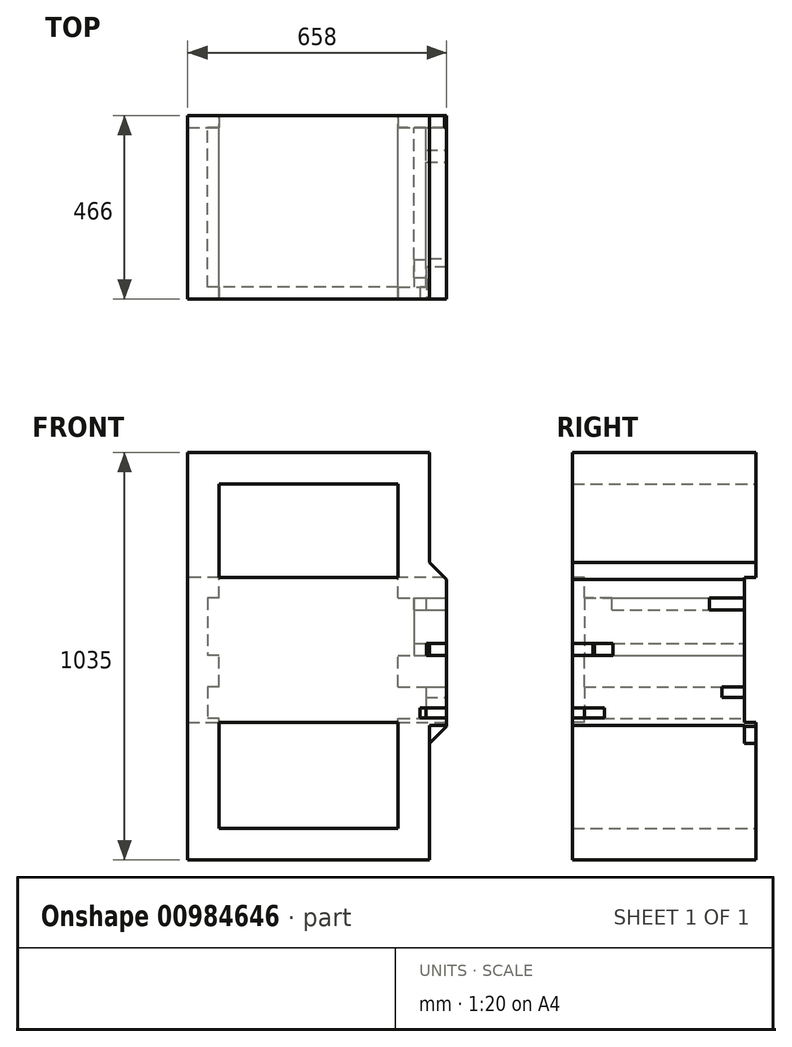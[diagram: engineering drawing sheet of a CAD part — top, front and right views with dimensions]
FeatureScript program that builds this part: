
annotation { "Feature Type Name" : "Feature", "Feature Type Description" : "" }
export const myFeature = defineFeature(function(context is Context, id is Id, definition is map)
    precondition{}
    {
        {
            var Q0;
            Q0=qCreatedBy(makeId("Front.planeOp"),FACE);
            var sketch = newSketch(context, id + "F0", { "sketchPlane" : qUnion([Q0])});
            skLineSegment(sketch, "E0", {"start": v(-307.5, 0) * mm, "end": v(307.5, 0) * mm});
            skLineSegment(sketch, "E1", {"start": v(-307.5, 0) * mm, "end": v(-307.5, 1035) * mm});
            skLineSegment(sketch, "E2", {"start": v(-307.5, 1035) * mm, "end": v(307.5, 1035) * mm});
            skLineSegment(sketch, "E3", {"start": v(307.5, 1035) * mm, "end": v(307.5, 0) * mm});
            skLineSegment(sketch, "E4.bottom", {"start": v(-227.5, 80) * mm, "end": v(227.5, 80) * mm});
            skLineSegment(sketch, "E4.top", {"start": v(-227.5, 955) * mm, "end": v(227.5, 955) * mm});
            skLineSegment(sketch, "E4.left", {"start": v(-227.5, 80) * mm, "end": v(-227.5, 360) * mm});
            skLineSegment(sketch, "E4.right", {"start": v(227.5, 80) * mm, "end": v(227.5, 360) * mm});
            skLineSegment(sketch, "E5.bottom", {"start": v(-227.5, 665) * mm, "end": v(-257.5, 665) * mm});
            skLineSegment(sketch, "E5.top", {"start": v(-227.5, 520) * mm, "end": v(-257.5, 520) * mm});
            skLineSegment(sketch, "E5.right", {"start": v(-257.5, 665) * mm, "end": v(-257.5, 520) * mm});
            skLineSegment(sketch, "E6.bottom", {"start": v(227.5, 665) * mm, "end": v(267.5, 665) * mm});
            skLineSegment(sketch, "E6.top", {"start": v(227.5, 520) * mm, "end": v(267.5, 520) * mm});
            skLineSegment(sketch, "E6.right", {"start": v(267.5, 635) * mm, "end": v(267.5, 550) * mm});
            skLineSegment(sketch, "E7.trimOffspring", {"start": v(227.5, 665) * mm, "end": v(227.5, 955) * mm});
            skLineSegment(sketch, "E8.trimOffspring", {"start": v(-227.5, 665) * mm, "end": v(-227.5, 955) * mm});
            skLineSegment(sketch, "E9.bottom", {"start": v(227.5, 440) * mm, "end": v(297.5, 440) * mm});
            skLineSegment(sketch, "E9.top", {"start": v(227.5, 360) * mm, "end": v(297.5, 360) * mm});
            skLineSegment(sketch, "E9.right", {"start": v(297.5, 440) * mm, "end": v(297.5, 360) * mm});
            skLineSegment(sketch, "E10.bottom", {"start": v(-227.5, 440) * mm, "end": v(-257.5, 440) * mm});
            skLineSegment(sketch, "E10.top", {"start": v(-227.5, 360) * mm, "end": v(-257.5, 360) * mm});
            skLineSegment(sketch, "E10.right", {"start": v(-257.5, 440) * mm, "end": v(-257.5, 360) * mm});
            skLineSegment(sketch, "E11.trimOffspring", {"start": v(227.5, 440) * mm, "end": v(227.5, 520) * mm});
            skLineSegment(sketch, "E12.trimOffspring", {"start": v(-227.5, 440) * mm, "end": v(-227.5, 520) * mm});
            skLineSegment(sketch, "E13.bottom", {"start": v(267.5, 665) * mm, "end": v(297.5, 665) * mm});
            skLineSegment(sketch, "E13.top", {"start": v(267.5, 635) * mm, "end": v(297.5, 635) * mm});
            skLineSegment(sketch, "E13.right", {"start": v(297.5, 665) * mm, "end": v(297.5, 635) * mm});
            skLineSegment(sketch, "E14.bottom", {"start": v(267.5, 550) * mm, "end": v(297.5, 550) * mm});
            skLineSegment(sketch, "E14.top", {"start": v(267.5, 520) * mm, "end": v(297.5, 520) * mm});
            skLineSegment(sketch, "E14.right", {"start": v(297.5, 550) * mm, "end": v(297.5, 520) * mm});
            skLineSegment(sketch, "E15.trimOffspring", {"start": v(267.5, 520) * mm, "end": v(267.5, 520) * mm});
            skSolve(sketch);
        }
        {
            var Q0;
            Q0=makeQuery(id+"F0.imprint","IMPRINT",FACE,{"disambiguationData":[TD([[makeQuery(id+"F0.imprint","IMPRINT",EDGE,{"derivedFrom":sQuery(id+"F0.wireOp",EDGE,"E0")}),1.0]])]});
            extrude(context, id + "F1", {"entities" : qUnion([Q0]), "depth" : 436 * mm, "offsetDistance" : 25 * mm});
        }
        {
            var Q0;
            Q0=makeQuery(id+"F1.opExtrude","SWEPT_FACE",FACE,{"disambiguationData":[OSD([sQuery(id+"F0.wireOp",EDGE,"E3")])]});
            var sketch = newSketch(context, id + "F2", { "sketchPlane" : qUnion([Q0])});
            skLineSegment(sketch, "E16.bottom", {"start": v(-383.78, 550) * mm, "end": v(0, 550) * mm});
            skLineSegment(sketch, "E16.top", {"start": v(-383.78, 520) * mm, "end": v(0, 520) * mm});
            skLineSegment(sketch, "E16.left", {"start": v(-383.78, 550) * mm, "end": v(-383.78, 520) * mm});
            skLineSegment(sketch, "E16.right", {"start": v(0, 550) * mm, "end": v(0, 520) * mm});
            skLineSegment(sketch, "E17.bottom", {"start": v(0, 665) * mm, "end": v(-88.2, 665) * mm});
            skLineSegment(sketch, "E17.top", {"start": v(0, 635) * mm, "end": v(-88.2, 635) * mm});
            skLineSegment(sketch, "E17.left", {"start": v(0, 665) * mm, "end": v(0, 635) * mm});
            skLineSegment(sketch, "E17.right", {"start": v(-88.2, 665) * mm, "end": v(-88.2, 635) * mm});
            skLineSegment(sketch, "E18.0", {"start": v(-436, 550) * mm, "end": v(0, 550) * mm});
            skLineSegment(sketch, "E19.0", {"start": v(-436, 520) * mm, "end": v(0, 520) * mm});
            skLineSegment(sketch, "E20.0", {"start": v(-436, 635) * mm, "end": v(0, 635) * mm});
            skLineSegment(sketch, "E21.0", {"start": v(-436, 665) * mm, "end": v(0, 665) * mm});
            skSolve(sketch);
        }
        {
            var Q0;
            Q0 = qSketchRegion(id + "F2", true);
            extrude(context, id + "F3", {"entities" : qUnion([Q0]), "operationType" : NewBodyOperationType.REMOVE, "endBound" : BoundingType.UP_TO_NEXT, "oppositeDirection" : true, "depth" : 25 * mm, "offsetDistance" : 25 * mm});
        }
        {
            var Q0;
            Q0=makeQuery(id+"F1.opExtrude","SWEPT_FACE",FACE,{"disambiguationData":[OSD([sQuery(id+"F0.wireOp",EDGE,"E3")])]});
            var sketch = newSketch(context, id + "F4", { "sketchPlane" : qUnion([Q0])});
            skLineSegment(sketch, "E22.bottom", {"start": v(-436, 710.09) * mm, "end": v(0, 710.09) * mm});
            skLineSegment(sketch, "E22.top", {"start": v(-436, 341.43) * mm, "end": v(0, 341.43) * mm});
            skLineSegment(sketch, "E22.left", {"start": v(-436, 710.09) * mm, "end": v(-436, 341.43) * mm});
            skLineSegment(sketch, "E22.right", {"start": v(0, 710.09) * mm, "end": v(0, 341.43) * mm});
            skSolve(sketch);
        }
        {
            var Q0;
            Q0 = qSketchRegion(id + "F4", true);
            extrude(context, id + "F5", {"entities" : qUnion([Q0]), "operationType" : NewBodyOperationType.ADD, "depth" : 43 * mm, "offsetDistance" : 25 * mm});
        }
        {
            var Q0;
            Q0=makeQuery(id+"F5.opExtrude","CAP_EDGE",EDGE,{"disambiguationData":[OSD([sQuery(id+"F4.wireOp",EDGE,"E22.bottom")])],"isStart":true});
            var Q1;
            Q1=makeQuery(id+"F5.opExtrude","CAP_EDGE",EDGE,{"disambiguationData":[OSD([sQuery(id+"F4.wireOp",EDGE,"E22.top")])],"isStart":true});
            chamfer(context, id + "F6", {"entities" : qUnion([Q0, Q1]), "width" : 45 * mm, "tangentPropagation" : true});
        }
        {
            var Q0;
            Q0=makeQuery(id+"F5.opExtrude","CAP_FACE",FACE,{"disambiguationData":[OSD([sQuery(id+"F4.wireOp",EDGE,"E22.bottom"),sQuery(id+"F4.wireOp",EDGE,"E22.top"),sQuery(id+"F4.wireOp",EDGE,"E22.left"),sQuery(id+"F4.wireOp",EDGE,"E22.right")])],"isStart":false});
            var sketch = newSketch(context, id + "F7", { "sketchPlane" : qUnion([Q0])});
            skLineSegment(sketch, "E23.0", {"start": v(-436, 550) * mm, "end": v(0, 550) * mm, "construction": true});
            skLineSegment(sketch, "E24.0", {"start": v(-436, 520) * mm, "end": v(0, 520) * mm, "construction": true});
            skLineSegment(sketch, "E25", {"start": v(-333.35, 550) * mm, "end": v(-436, 550) * mm});
            skLineSegment(sketch, "E26", {"start": v(-333.35, 520) * mm, "end": v(-436, 520) * mm});
            skLineSegment(sketch, "E27", {"start": v(-436, 520) * mm, "end": v(-436, 550) * mm});
            skLineSegment(sketch, "E28", {"start": v(-333.35, 520) * mm, "end": v(-333.35, 550) * mm});
            skLineSegment(sketch, "E29.0", {"start": v(-88.2, 665) * mm, "end": v(0, 665) * mm, "construction": true});
            skLineSegment(sketch, "E30.0", {"start": v(-88.2, 635) * mm, "end": v(0, 635) * mm, "construction": true});
            skLineSegment(sketch, "E31.0", {"start": v(-88.2, 665) * mm, "end": v(-88.2, 635) * mm, "construction": true});
            skLineSegment(sketch, "E32", {"start": v(-88.2, 665) * mm, "end": v(0, 665) * mm});
            skLineSegment(sketch, "E33", {"start": v(0, 665) * mm, "end": v(0, 635) * mm});
            skLineSegment(sketch, "E34", {"start": v(0, 635) * mm, "end": v(-88.2, 635) * mm});
            skLineSegment(sketch, "E35", {"start": v(-88.2, 635) * mm, "end": v(-88.2, 665) * mm});
            skLineSegment(sketch, "E36", {"start": v(0, 635) * mm, "end": v(0, 665) * mm});
            skSolve(sketch);
        }
        {
            var Q0;
            Q0=makeQuery(id+"F7.imprint","IMPRINT",FACE,{"disambiguationData":[TD([[makeQuery(id+"F7.imprint","IMPRINT",EDGE,{"derivedFrom":sQuery(id+"F7.wireOp",EDGE,"E25")}),1.0]])]});
            var Q1;
            {var subQ5=sQuery(id+"F7.wireOp",EDGE,"E34");Q1=makeQuery(id+"F7.imprint","IMPRINT",FACE,{"disambiguationData":[TD([[makeQuery(id+"F7.imprint","IMPRINT",EDGE,{"derivedFrom":subQ5}),-1.0]])]});}
            var Q2;
            {var subQ0=sQuery(id+"F7.wireOp",EDGE,"E36");var subQ1=sQuery(id+"F7.wireOp",EDGE,"E32");var subQ2=makeQuery(id+"F7.imprint","INTERSECT",VERTEX,{"derivedFrom":[subQ1,subQ0]});Q2=makeQuery(id+"F7.imprint","IMPRINT",FACE,{"disambiguationData":[TD([[makeQuery(id+"F7.imprint","IMPRINT",EDGE,{"disambiguationData":[TD([[subQ2,1.0]])],"derivedFrom":subQ1}),-1.0]])]});}
            extrude(context, id + "F8", {"entities" : qUnion([Q0, Q1, Q2]), "operationType" : NewBodyOperationType.REMOVE, "oppositeDirection" : true, "depth" : 51 * mm, "offsetDistance" : 25 * mm});
        }
        {
            var Q0;
            Q0=makeQuery(id+"F5.boolean.opBoolean","MERGE",FACE,{"derivedFrom":[makeQuery(id+"F1.opExtrude","CAP_FACE",FACE,{"disambiguationData":[OSD([sQuery(id+"F0.wireOp",EDGE,"E0"),sQuery(id+"F0.wireOp",EDGE,"E1"),sQuery(id+"F0.wireOp",EDGE,"E2"),sQuery(id+"F0.wireOp",EDGE,"E3"),sQuery(id+"F0.wireOp",EDGE,"E4.bottom"),sQuery(id+"F0.wireOp",EDGE,"E4.top"),sQuery(id+"F0.wireOp",EDGE,"E4.left"),sQuery(id+"F0.wireOp",EDGE,"E4.right"),sQuery(id+"F0.wireOp",EDGE,"E5.bottom"),sQuery(id+"F0.wireOp",EDGE,"E5.top"),sQuery(id+"F0.wireOp",EDGE,"E5.right"),sQuery(id+"F0.wireOp",EDGE,"E6.bottom"),sQuery(id+"F0.wireOp",EDGE,"E6.top"),sQuery(id+"F0.wireOp",EDGE,"E6.right"),sQuery(id+"F0.wireOp",EDGE,"E7.trimOffspring"),sQuery(id+"F0.wireOp",EDGE,"E8.trimOffspring"),sQuery(id+"F0.wireOp",EDGE,"E9.bottom"),sQuery(id+"F0.wireOp",EDGE,"E9.top"),sQuery(id+"F0.wireOp",EDGE,"E9.right"),sQuery(id+"F0.wireOp",EDGE,"E10.bottom"),sQuery(id+"F0.wireOp",EDGE,"E10.top"),sQuery(id+"F0.wireOp",EDGE,"E10.right"),sQuery(id+"F0.wireOp",EDGE,"E11.trimOffspring"),sQuery(id+"F0.wireOp",EDGE,"E12.trimOffspring"),sQuery(id+"F0.wireOp",EDGE,"E13.bottom"),sQuery(id+"F0.wireOp",EDGE,"E13.top"),sQuery(id+"F0.wireOp",EDGE,"E13.right"),sQuery(id+"F0.wireOp",EDGE,"E14.bottom"),sQuery(id+"F0.wireOp",EDGE,"E14.top"),sQuery(id+"F0.wireOp",EDGE,"E14.right")])],"isStart":false}),makeQuery(id+"F5.opExtrude","SWEPT_FACE",FACE,{"disambiguationData":[OSD([sQuery(id+"F4.wireOp",EDGE,"E22.left")])]})]});
            var sketch = newSketch(context, id + "F9", { "sketchPlane" : qUnion([Q0])});
            skLineSegment(sketch, "E37.bottom", {"start": v(297.5, 550) * mm, "end": v(267.5, 550) * mm});
            skLineSegment(sketch, "E37.top", {"start": v(297.5, 520) * mm, "end": v(267.5, 520) * mm});
            skLineSegment(sketch, "E37.left", {"start": v(297.5, 550) * mm, "end": v(297.5, 520) * mm});
            skLineSegment(sketch, "E37.right", {"start": v(267.5, 550) * mm, "end": v(267.5, 520) * mm});
            skSolve(sketch);
        }
        {
            var Q0;
            Q0 = qSketchRegion(id + "F9", true);
            extrude(context, id + "F10", {"entities" : qUnion([Q0]), "operationType" : NewBodyOperationType.ADD, "oppositeDirection" : true, "depth" : 55 * mm, "offsetDistance" : 25 * mm});
        }
        {
            var Q0;
            Q0=makeQuery(id+"F10.boolean.opBoolean","MERGE",FACE,{"derivedFrom":[makeQuery(id+"F5.boolean.opBoolean","MERGE",FACE,{"derivedFrom":[makeQuery(id+"F1.opExtrude","CAP_FACE",FACE,{"disambiguationData":[OSD([sQuery(id+"F0.wireOp",EDGE,"E0"),sQuery(id+"F0.wireOp",EDGE,"E1"),sQuery(id+"F0.wireOp",EDGE,"E2"),sQuery(id+"F0.wireOp",EDGE,"E3"),sQuery(id+"F0.wireOp",EDGE,"E4.bottom"),sQuery(id+"F0.wireOp",EDGE,"E4.top"),sQuery(id+"F0.wireOp",EDGE,"E4.left"),sQuery(id+"F0.wireOp",EDGE,"E4.right"),sQuery(id+"F0.wireOp",EDGE,"E5.bottom"),sQuery(id+"F0.wireOp",EDGE,"E5.top"),sQuery(id+"F0.wireOp",EDGE,"E5.right"),sQuery(id+"F0.wireOp",EDGE,"E6.bottom"),sQuery(id+"F0.wireOp",EDGE,"E6.top"),sQuery(id+"F0.wireOp",EDGE,"E6.right"),sQuery(id+"F0.wireOp",EDGE,"E7.trimOffspring"),sQuery(id+"F0.wireOp",EDGE,"E8.trimOffspring"),sQuery(id+"F0.wireOp",EDGE,"E9.bottom"),sQuery(id+"F0.wireOp",EDGE,"E9.top"),sQuery(id+"F0.wireOp",EDGE,"E9.right"),sQuery(id+"F0.wireOp",EDGE,"E10.bottom"),sQuery(id+"F0.wireOp",EDGE,"E10.top"),sQuery(id+"F0.wireOp",EDGE,"E10.right"),sQuery(id+"F0.wireOp",EDGE,"E11.trimOffspring"),sQuery(id+"F0.wireOp",EDGE,"E12.trimOffspring"),sQuery(id+"F0.wireOp",EDGE,"E13.bottom"),sQuery(id+"F0.wireOp",EDGE,"E13.top"),sQuery(id+"F0.wireOp",EDGE,"E13.right"),sQuery(id+"F0.wireOp",EDGE,"E14.bottom"),sQuery(id+"F0.wireOp",EDGE,"E14.top"),sQuery(id+"F0.wireOp",EDGE,"E14.right")])],"isStart":false}),makeQuery(id+"F5.opExtrude","SWEPT_FACE",FACE,{"disambiguationData":[OSD([sQuery(id+"F4.wireOp",EDGE,"E22.left")])]})]}),makeQuery(id+"F10.opExtrude","CAP_FACE",FACE,{"disambiguationData":[OSD([sQuery(id+"F9.wireOp",EDGE,"E37.bottom"),sQuery(id+"F9.wireOp",EDGE,"E37.top"),sQuery(id+"F9.wireOp",EDGE,"E37.left"),sQuery(id+"F9.wireOp",EDGE,"E37.right")])],"isStart":true})]});
            var sketch = newSketch(context, id + "F11", { "sketchPlane" : qUnion([Q0])});
            skLineSegment(sketch, "E38.0", {"start": v(267.5, 635) * mm, "end": v(297.5, 635) * mm});
            skLineSegment(sketch, "E39.0", {"start": v(297.5, 665) * mm, "end": v(297.5, 635) * mm});
            skLineSegment(sketch, "E40", {"start": v(267.5, 635) * mm, "end": v(267.5, 665) * mm});
            skLineSegment(sketch, "E41", {"start": v(267.5, 665) * mm, "end": v(297.5, 665) * mm});
            skSolve(sketch);
        }
        {
            var Q0;
            Q0=makeQuery(id+"F11.imprint","IMPRINT",FACE,{"disambiguationData":[TD([[makeQuery(id+"F11.imprint","IMPRINT",EDGE,{"derivedFrom":sQuery(id+"F11.wireOp",EDGE,"E38.0")}),1.0]])]});
            extrude(context, id + "F12", {"entities" : qUnion([Q0]), "operationType" : NewBodyOperationType.ADD, "oppositeDirection" : true, "depth" : 100 * mm, "offsetDistance" : 25 * mm});
        }
        {
            var Q0;
            Q0=makeQuery(id+"F12.boolean.opBoolean","MERGE",FACE,{"derivedFrom":[makeQuery(id+"F10.boolean.opBoolean","MERGE",FACE,{"derivedFrom":[makeQuery(id+"F5.boolean.opBoolean","MERGE",FACE,{"derivedFrom":[makeQuery(id+"F1.opExtrude","CAP_FACE",FACE,{"disambiguationData":[OSD([sQuery(id+"F0.wireOp",EDGE,"E0"),sQuery(id+"F0.wireOp",EDGE,"E1"),sQuery(id+"F0.wireOp",EDGE,"E2"),sQuery(id+"F0.wireOp",EDGE,"E3"),sQuery(id+"F0.wireOp",EDGE,"E4.bottom"),sQuery(id+"F0.wireOp",EDGE,"E4.top"),sQuery(id+"F0.wireOp",EDGE,"E4.left"),sQuery(id+"F0.wireOp",EDGE,"E4.right"),sQuery(id+"F0.wireOp",EDGE,"E5.bottom"),sQuery(id+"F0.wireOp",EDGE,"E5.top"),sQuery(id+"F0.wireOp",EDGE,"E5.right"),sQuery(id+"F0.wireOp",EDGE,"E6.bottom"),sQuery(id+"F0.wireOp",EDGE,"E6.top"),sQuery(id+"F0.wireOp",EDGE,"E6.right"),sQuery(id+"F0.wireOp",EDGE,"E7.trimOffspring"),sQuery(id+"F0.wireOp",EDGE,"E8.trimOffspring"),sQuery(id+"F0.wireOp",EDGE,"E9.bottom"),sQuery(id+"F0.wireOp",EDGE,"E9.top"),sQuery(id+"F0.wireOp",EDGE,"E9.right"),sQuery(id+"F0.wireOp",EDGE,"E10.bottom"),sQuery(id+"F0.wireOp",EDGE,"E10.top"),sQuery(id+"F0.wireOp",EDGE,"E10.right"),sQuery(id+"F0.wireOp",EDGE,"E11.trimOffspring"),sQuery(id+"F0.wireOp",EDGE,"E12.trimOffspring"),sQuery(id+"F0.wireOp",EDGE,"E13.bottom"),sQuery(id+"F0.wireOp",EDGE,"E13.top"),sQuery(id+"F0.wireOp",EDGE,"E13.right"),sQuery(id+"F0.wireOp",EDGE,"E14.bottom"),sQuery(id+"F0.wireOp",EDGE,"E14.top"),sQuery(id+"F0.wireOp",EDGE,"E14.right")])],"isStart":false}),makeQuery(id+"F5.opExtrude","SWEPT_FACE",FACE,{"disambiguationData":[OSD([sQuery(id+"F4.wireOp",EDGE,"E22.left")])]})]}),makeQuery(id+"F10.opExtrude","CAP_FACE",FACE,{"disambiguationData":[OSD([sQuery(id+"F9.wireOp",EDGE,"E37.bottom"),sQuery(id+"F9.wireOp",EDGE,"E37.top"),sQuery(id+"F9.wireOp",EDGE,"E37.left"),sQuery(id+"F9.wireOp",EDGE,"E37.right")])],"isStart":true})]}),makeQuery(id+"F12.opExtrude","CAP_FACE",FACE,{"disambiguationData":[OSD([sQuery(id+"F11.wireOp",EDGE,"E38.0"),sQuery(id+"F11.wireOp",EDGE,"E39.0"),sQuery(id+"F11.wireOp",EDGE,"E40"),sQuery(id+"F11.wireOp",EDGE,"E41")])],"isStart":true})]});
            var sketch = newSketch(context, id + "F13", { "sketchPlane" : qUnion([Q0])});
            skLineSegment(sketch, "E42.bottom", {"start": v(297.82, 717.92) * mm, "end": v(-289.37, 717.92) * mm});
            skLineSegment(sketch, "E42.top", {"start": v(297.82, 348.85) * mm, "end": v(-289.37, 348.85) * mm});
            skLineSegment(sketch, "E42.left", {"start": v(297.82, 717.92) * mm, "end": v(297.82, 348.85) * mm});
            skLineSegment(sketch, "E42.right", {"start": v(-289.37, 717.92) * mm, "end": v(-289.37, 348.85) * mm});
            skSolve(sketch);
        }
        {
            var Q0;
            {var subQ2=makeQuery(id+"F1.opExtrude","CAP_EDGE",EDGE,{"disambiguationData":[OSD([sQuery(id+"F0.wireOp",EDGE,"E5.bottom")])],"isStart":false});Q0=makeQuery(id+"F13.imprint","IMPRINT",FACE,{"disambiguationData":[TD([[makeQuery(id+"F13.imprint","IMPRINT",EDGE,{"derivedFrom":subQ2}),1.0]])]});}
            extrude(context, id + "F14", {"entities" : qUnion([Q0]), "operationType" : NewBodyOperationType.ADD, "oppositeDirection" : true, "depth" : 30 * mm, "offsetDistance" : 25 * mm});
        }
        {
            var Q0;
            {var subQ0=sQuery(id+"F0.wireOp",EDGE,"E11.trimOffspring");var subQ1=sQuery(id+"F0.wireOp",EDGE,"E10.top");var subQ2=sQuery(id+"F0.wireOp",EDGE,"E10.bottom");var subQ3=sQuery(id+"F0.wireOp",EDGE,"E9.right");var subQ4=sQuery(id+"F0.wireOp",EDGE,"E9.top");var subQ5=sQuery(id+"F0.wireOp",EDGE,"E9.bottom");var subQ6=sQuery(id+"F0.wireOp",EDGE,"E8.trimOffspring");var subQ7=sQuery(id+"F0.wireOp",EDGE,"E7.trimOffspring");var subQ8=sQuery(id+"F0.wireOp",EDGE,"E14.top");var subQ9=sQuery(id+"F0.wireOp",EDGE,"E6.top");var subQ10=sQuery(id+"F0.wireOp",EDGE,"E13.bottom");var subQ11=sQuery(id+"F0.wireOp",EDGE,"E6.bottom");var subQ12=sQuery(id+"F0.wireOp",EDGE,"E5.right");var subQ13=sQuery(id+"F0.wireOp",EDGE,"E2");var subQ14=sQuery(id+"F0.wireOp",EDGE,"E1");var subQ15=sQuery(id+"F0.wireOp",EDGE,"E3");var subQ17=sQuery(id+"F0.wireOp",EDGE,"E10.right");var subQ18=sQuery(id+"F0.wireOp",EDGE,"E0");var subQ19=sQuery(id+"F0.wireOp",EDGE,"E5.top");var subQ20=sQuery(id+"F0.wireOp",EDGE,"E4.bottom");var subQ21=sQuery(id+"F0.wireOp",EDGE,"E4.top");var subQ22=sQuery(id+"F0.wireOp",EDGE,"E4.left");var subQ23=sQuery(id+"F0.wireOp",EDGE,"E4.right");var subQ24=sQuery(id+"F0.wireOp",EDGE,"E5.bottom");var subQ25=sQuery(id+"F0.wireOp",EDGE,"E12.trimOffspring");var subQ26=sQuery(id+"F0.wireOp",EDGE,"E14.bottom");var subQ27=sQuery(id+"F0.wireOp",EDGE,"E13.top");var subQ28=sQuery(id+"F0.wireOp",EDGE,"E6.right");var subQ29=makeQuery(id+"F1.opExtrude","CAP_FACE",FACE,{"disambiguationData":[OSD([subQ18,subQ14,subQ13,subQ15,subQ20,subQ21,subQ22,subQ23,subQ24,subQ19,subQ12,subQ11,subQ9,subQ28,subQ7,subQ6,subQ5,subQ4,subQ3,subQ2,subQ1,subQ17,subQ0,subQ25,subQ10,subQ27,sQuery(id+"F0.wireOp",EDGE,"E13.right"),subQ26,subQ8,sQuery(id+"F0.wireOp",EDGE,"E14.right")])],"isStart":true});Q0=makeQuery(id+"F5.boolean.opBoolean","MERGE",FACE,{"derivedFrom":[makeQuery(id+"F3.boolean.opBoolean","SPLIT",FACE,{"disambiguationData":[TD([makeQuery(id+"F1.opExtrude","SWEPT_FACE",FACE,{"disambiguationData":[OSD([subQ28])]})])],"derivedFrom":subQ29}),makeQuery(id+"F3.boolean.opBoolean","SPLIT",FACE,{"disambiguationData":[TD([makeQuery(id+"F1.opExtrude","SWEPT_FACE",FACE,{"disambiguationData":[OSD([subQ18])]})])],"derivedFrom":subQ29}),makeQuery(id+"F5.opExtrude","SWEPT_FACE",FACE,{"disambiguationData":[OSD([sQuery(id+"F4.wireOp",EDGE,"E22.right")])]})]});}
            var sketch = newSketch(context, id + "F15", { "sketchPlane" : qUnion([Q0])});
            skLineSegment(sketch, "E43.bottom", {"start": v(-297.5, 440) * mm, "end": v(-350.5, 440) * mm});
            skLineSegment(sketch, "E43.top", {"start": v(-297.5, 412.74) * mm, "end": v(-350.5, 412.74) * mm});
            skLineSegment(sketch, "E43.left", {"start": v(-297.5, 440) * mm, "end": v(-297.5, 412.74) * mm});
            skLineSegment(sketch, "E43.right", {"start": v(-350.5, 440) * mm, "end": v(-350.5, 412.74) * mm});
            skSolve(sketch);
        }
        {
            var Q0;
            Q0=makeQuery(id+"F15.imprint","IMPRINT",FACE,{"disambiguationData":[TD([[makeQuery(id+"F15.imprint","IMPRINT",EDGE,{"derivedFrom":sQuery(id+"F15.wireOp",EDGE,"E43.bottom")}),1.0]])]});
            extrude(context, id + "F16", {"entities" : qUnion([Q0]), "operationType" : NewBodyOperationType.REMOVE, "oppositeDirection" : true, "depth" : 57 * mm, "offsetDistance" : 25 * mm});
        }
        {
            var Q0;
            {var subQ0=sQuery(id+"F11.wireOp",EDGE,"E40");var subQ1=sQuery(id+"F9.wireOp",EDGE,"E37.right");var subQ2=sQuery(id+"F0.wireOp",EDGE,"E14.top");var subQ3=sQuery(id+"F0.wireOp",EDGE,"E13.bottom");var subQ4=sQuery(id+"F0.wireOp",EDGE,"E12.trimOffspring");var subQ5=sQuery(id+"F0.wireOp",EDGE,"E11.trimOffspring");var subQ6=sQuery(id+"F0.wireOp",EDGE,"E10.right");var subQ7=sQuery(id+"F0.wireOp",EDGE,"E10.top");var subQ8=sQuery(id+"F0.wireOp",EDGE,"E10.bottom");var subQ9=sQuery(id+"F0.wireOp",EDGE,"E9.right");var subQ10=sQuery(id+"F0.wireOp",EDGE,"E9.top");var subQ11=sQuery(id+"F0.wireOp",EDGE,"E9.bottom");var subQ12=sQuery(id+"F0.wireOp",EDGE,"E8.trimOffspring");var subQ13=sQuery(id+"F0.wireOp",EDGE,"E7.trimOffspring");var subQ14=sQuery(id+"F0.wireOp",EDGE,"E6.right");var subQ15=sQuery(id+"F0.wireOp",EDGE,"E6.top");var subQ16=sQuery(id+"F0.wireOp",EDGE,"E6.bottom");var subQ17=sQuery(id+"F0.wireOp",EDGE,"E5.right");var subQ18=sQuery(id+"F0.wireOp",EDGE,"E5.top");var subQ19=sQuery(id+"F0.wireOp",EDGE,"E5.bottom");var subQ20=sQuery(id+"F0.wireOp",EDGE,"E4.right");var subQ21=sQuery(id+"F0.wireOp",EDGE,"E4.left");Q0=makeQuery(id+"F14.boolean.opBoolean","MERGE",FACE,{"derivedFrom":[makeQuery(id+"F12.boolean.opBoolean","MERGE",FACE,{"derivedFrom":[makeQuery(id+"F10.boolean.opBoolean","MERGE",FACE,{"derivedFrom":[makeQuery(id+"F5.boolean.opBoolean","MERGE",FACE,{"derivedFrom":[makeQuery(id+"F1.opExtrude","CAP_FACE",FACE,{"disambiguationData":[OSD([sQuery(id+"F0.wireOp",EDGE,"E0"),sQuery(id+"F0.wireOp",EDGE,"E1"),sQuery(id+"F0.wireOp",EDGE,"E2"),sQuery(id+"F0.wireOp",EDGE,"E3"),sQuery(id+"F0.wireOp",EDGE,"E4.bottom"),sQuery(id+"F0.wireOp",EDGE,"E4.top"),subQ21,subQ20,subQ19,subQ18,subQ17,subQ16,subQ15,subQ14,subQ13,subQ12,subQ11,subQ10,subQ9,subQ8,subQ7,subQ6,subQ5,subQ4,subQ3,sQuery(id+"F0.wireOp",EDGE,"E13.top"),sQuery(id+"F0.wireOp",EDGE,"E13.right"),sQuery(id+"F0.wireOp",EDGE,"E14.bottom"),subQ2,sQuery(id+"F0.wireOp",EDGE,"E14.right")])],"isStart":false}),makeQuery(id+"F5.opExtrude","SWEPT_FACE",FACE,{"disambiguationData":[OSD([sQuery(id+"F4.wireOp",EDGE,"E22.left")])]})]}),makeQuery(id+"F10.opExtrude","CAP_FACE",FACE,{"disambiguationData":[OSD([sQuery(id+"F9.wireOp",EDGE,"E37.bottom"),sQuery(id+"F9.wireOp",EDGE,"E37.top"),sQuery(id+"F9.wireOp",EDGE,"E37.left"),subQ1])],"isStart":true})]}),makeQuery(id+"F12.opExtrude","CAP_FACE",FACE,{"disambiguationData":[OSD([sQuery(id+"F11.wireOp",EDGE,"E38.0"),sQuery(id+"F11.wireOp",EDGE,"E39.0"),subQ0,sQuery(id+"F11.wireOp",EDGE,"E41")])],"isStart":true})]}),makeQuery(id+"F14.opExtrude","CAP_FACE",FACE,{"disambiguationData":[OSD([subQ21,subQ20,subQ19,subQ18,subQ17,subQ16,subQ15,subQ14,subQ13,subQ12,subQ11,subQ10,subQ9,subQ8,subQ7,subQ6,subQ5,subQ4,subQ3,subQ2,subQ1,subQ0,sQuery(id+"F13.wireOp",EDGE,"E42.bottom"),sQuery(id+"F13.wireOp",EDGE,"E42.top")])],"isStart":true})]});}
            var sketch = newSketch(context, id + "F17", { "sketchPlane" : qUnion([Q0])});
            skLineSegment(sketch, "E44.bottom", {"start": v(350.5, 361.17) * mm, "end": v(282.57, 361.17) * mm});
            skLineSegment(sketch, "E44.top", {"start": v(350.5, 386.53) * mm, "end": v(282.57, 386.53) * mm});
            skLineSegment(sketch, "E44.left", {"start": v(350.5, 361.17) * mm, "end": v(350.5, 386.53) * mm});
            skLineSegment(sketch, "E44.right", {"start": v(282.57, 361.17) * mm, "end": v(282.57, 386.53) * mm});
            skSolve(sketch);
        }
        {
            var Q0;
            Q0=makeQuery(id+"F17.imprint","IMPRINT",FACE,{"disambiguationData":[TD([[makeQuery(id+"F17.imprint","IMPRINT",EDGE,{"derivedFrom":sQuery(id+"F17.wireOp",EDGE,"E44.bottom")}),-1.0]])]});
            extrude(context, id + "F18", {"entities" : qUnion([Q0]), "operationType" : NewBodyOperationType.REMOVE, "oppositeDirection" : true, "depth" : 81 * mm, "offsetDistance" : 25 * mm});
        }
        {
            var Q0;
            {var subQ0=sQuery(id+"F0.wireOp",EDGE,"E12.trimOffspring");var subQ2=sQuery(id+"F0.wireOp",EDGE,"E10.top");var subQ4=sQuery(id+"F0.wireOp",EDGE,"E10.bottom");var subQ6=sQuery(id+"F0.wireOp",EDGE,"E9.right");var subQ8=sQuery(id+"F4.wireOp",EDGE,"E22.right");var subQ11=sQuery(id+"F0.wireOp",EDGE,"E9.top");var subQ13=sQuery(id+"F0.wireOp",EDGE,"E8.trimOffspring");var subQ15=sQuery(id+"F0.wireOp",EDGE,"E7.trimOffspring");var subQ17=sQuery(id+"F0.wireOp",EDGE,"E13.bottom");var subQ18=sQuery(id+"F0.wireOp",EDGE,"E6.bottom");var subQ20=sQuery(id+"F0.wireOp",EDGE,"E5.right");var subQ22=sQuery(id+"F0.wireOp",EDGE,"E2");var subQ24=sQuery(id+"F0.wireOp",EDGE,"E1");var subQ26=sQuery(id+"F0.wireOp",EDGE,"E3");var subQ28=sQuery(id+"F0.wireOp",EDGE,"E10.right");var subQ30=sQuery(id+"F0.wireOp",EDGE,"E0");var subQ31=makeQuery(id+"F1.opExtrude","SWEPT_FACE",FACE,{"disambiguationData":[OSD([subQ30])]});var subQ32=sQuery(id+"F0.wireOp",EDGE,"E5.top");var subQ34=sQuery(id+"F0.wireOp",EDGE,"E4.bottom");var subQ36=sQuery(id+"F0.wireOp",EDGE,"E4.top");var subQ38=sQuery(id+"F0.wireOp",EDGE,"E4.left");var subQ40=sQuery(id+"F0.wireOp",EDGE,"E4.right");var subQ42=sQuery(id+"F0.wireOp",EDGE,"E5.bottom");var subQ44=sQuery(id+"F0.wireOp",EDGE,"E11.trimOffspring");var subQ45=sQuery(id+"F0.wireOp",EDGE,"E9.bottom");var subQ46=sQuery(id+"F0.wireOp",EDGE,"E14.top");var subQ47=sQuery(id+"F0.wireOp",EDGE,"E6.top");var subQ48=sQuery(id+"F0.wireOp",EDGE,"E14.bottom");var subQ49=sQuery(id+"F0.wireOp",EDGE,"E13.top");var subQ50=sQuery(id+"F0.wireOp",EDGE,"E6.right");var subQ51=makeQuery(id+"F1.opExtrude","CAP_FACE",FACE,{"disambiguationData":[OSD([subQ30,subQ24,subQ22,subQ26,subQ34,subQ36,subQ38,subQ40,subQ42,subQ32,subQ20,subQ18,subQ47,subQ50,subQ15,subQ13,subQ45,subQ11,subQ6,subQ4,subQ2,subQ28,subQ44,subQ0,subQ17,subQ49,sQuery(id+"F0.wireOp",EDGE,"E13.right"),subQ48,subQ46,sQuery(id+"F0.wireOp",EDGE,"E14.right")])],"isStart":true});Q0=makeQuery(id+"F16.boolean.opBoolean","SPLIT",FACE,{"disambiguationData":[TD([subQ31])],"derivedFrom":makeQuery(id+"F5.boolean.opBoolean","MERGE",FACE,{"derivedFrom":[makeQuery(id+"F3.boolean.opBoolean","SPLIT",FACE,{"disambiguationData":[TD([makeQuery(id+"F1.opExtrude","SWEPT_FACE",FACE,{"disambiguationData":[OSD([subQ50])]})])],"derivedFrom":subQ51}),makeQuery(id+"F3.boolean.opBoolean","SPLIT",FACE,{"disambiguationData":[TD([subQ31])],"derivedFrom":subQ51}),makeQuery(id+"F5.opExtrude","SWEPT_FACE",FACE,{"disambiguationData":[OSD([subQ8])]})]})});}
            var sketch = newSketch(context, id + "F19", { "sketchPlane" : qUnion([Q0])});
            skLineSegment(sketch, "E45.0", {"start": v(-227.5, 348.85) * mm, "end": v(227.5, 348.85) * mm, "construction": true});
            skLineSegment(sketch, "E46.0", {"start": v(-227.5, 717.92) * mm, "end": v(227.5, 717.92) * mm, "construction": true});
            skLineSegment(sketch, "E47", {"start": v(-227.5, 717.92) * mm, "end": v(-227.5, 955) * mm});
            skLineSegment(sketch, "E48", {"start": v(-227.5, 955) * mm, "end": v(227.5, 955) * mm});
            skLineSegment(sketch, "E49", {"start": v(227.5, 955) * mm, "end": v(227.5, 717.92) * mm});
            skLineSegment(sketch, "E50", {"start": v(227.5, 717.92) * mm, "end": v(307.5, 717.92) * mm});
            skLineSegment(sketch, "E51", {"start": v(307.5, 717.92) * mm, "end": v(307.5, 1035) * mm});
            skLineSegment(sketch, "E52", {"start": v(307.5, 1035) * mm, "end": v(-307.5, 1035) * mm});
            skLineSegment(sketch, "E53", {"start": v(-307.5, 1035) * mm, "end": v(-307.5, 755.09) * mm});
            skLineSegment(sketch, "E54", {"start": v(-307.5, 755.09) * mm, "end": v(-350.5, 712.09) * mm});
            skLineSegment(sketch, "E55", {"start": v(-350.5, 717.92) * mm, "end": v(-350.5, 712.09) * mm});
            skLineSegment(sketch, "E56", {"start": v(-350.5, 717.92) * mm, "end": v(-227.5, 717.92) * mm});
            skLineSegment(sketch, "E57", {"start": v(-227.5, 348.85) * mm, "end": v(-359.91, 348.85) * mm});
            skLineSegment(sketch, "E58", {"start": v(-359.91, 348.85) * mm, "end": v(-307.5, 296.43) * mm});
            skLineSegment(sketch, "E59", {"start": v(-307.5, 296.43) * mm, "end": v(-307.5, 0) * mm});
            skLineSegment(sketch, "E60", {"start": v(-307.5, 0) * mm, "end": v(307.5, 0) * mm});
            skLineSegment(sketch, "E61", {"start": v(307.5, 0) * mm, "end": v(307.5, 348.85) * mm});
            skLineSegment(sketch, "E62", {"start": v(307.5, 348.85) * mm, "end": v(227.5, 348.85) * mm});
            skLineSegment(sketch, "E63", {"start": v(227.5, 348.85) * mm, "end": v(227.5, 80) * mm});
            skLineSegment(sketch, "E64", {"start": v(227.5, 80) * mm, "end": v(-227.5, 80) * mm});
            skLineSegment(sketch, "E65", {"start": v(-227.5, 80) * mm, "end": v(-227.5, 348.85) * mm});
            skSolve(sketch);
        }
        {
            var Q0;
            Q0=makeQuery(id+"F19.imprint","IMPRINT",FACE,{"disambiguationData":[TD([[makeQuery(id+"F19.imprint","IMPRINT",EDGE,{"derivedFrom":sQuery(id+"F19.wireOp",EDGE,"E57")}),1.0]])]});
            var Q1;
            Q1=makeQuery(id+"F19.imprint","IMPRINT",FACE,{"disambiguationData":[TD([[makeQuery(id+"F19.imprint","IMPRINT",EDGE,{"derivedFrom":sQuery(id+"F19.wireOp",EDGE,"E47")}),1.0]])]});
            var Q2;
            {var subQ0=sQuery(id+"F19.wireOp",EDGE,"E59");Q2=makeQuery(id+"F19.imprint","IMPRINT",FACE,{"disambiguationData":[TD([[makeQuery(id+"F19.imprint","IMPRINT",EDGE,{"derivedFrom":subQ0}),1.0]])]});}
            extrude(context, id + "F20", {"entities" : qUnion([Q0, Q1, Q2]), "operationType" : NewBodyOperationType.ADD, "depth" : 30 * mm, "offsetDistance" : 25 * mm});
        }
        {
            var Q0;
            Q0=makeQuery(id+"F5.opExtrude","CAP_FACE",FACE,{"disambiguationData":[OSD([sQuery(id+"F4.wireOp",EDGE,"E22.bottom"),sQuery(id+"F4.wireOp",EDGE,"E22.top"),sQuery(id+"F4.wireOp",EDGE,"E22.left"),sQuery(id+"F4.wireOp",EDGE,"E22.right")])],"isStart":false});
            var sketch = newSketch(context, id + "F21", { "sketchPlane" : qUnion([Q0])});
            skLineSegment(sketch, "E66.bottom", {"start": v(-23.27, 373.7) * mm, "end": v(52.29, 373.7) * mm});
            skLineSegment(sketch, "E66.top", {"start": v(-23.27, 317.81) * mm, "end": v(52.29, 317.81) * mm});
            skLineSegment(sketch, "E66.left", {"start": v(-23.27, 373.7) * mm, "end": v(-23.27, 317.81) * mm});
            skLineSegment(sketch, "E66.right", {"start": v(52.29, 373.7) * mm, "end": v(52.29, 317.81) * mm});
            skSolve(sketch);
        }
        {
            var Q0;
            {var subQ2=sQuery(id+"F21.wireOp",EDGE,"E66.top");Q0=makeQuery(id+"F21.imprint","IMPRINT",FACE,{"disambiguationData":[TD([[makeQuery(id+"F21.imprint","IMPRINT",EDGE,{"derivedFrom":subQ2}),1.0]])]});}
            extrude(context, id + "F22", {"entities" : qUnion([Q0]), "operationType" : NewBodyOperationType.REMOVE, "depth" : 25 * mm, "offsetDistance" : 25 * mm});
        }
    });
